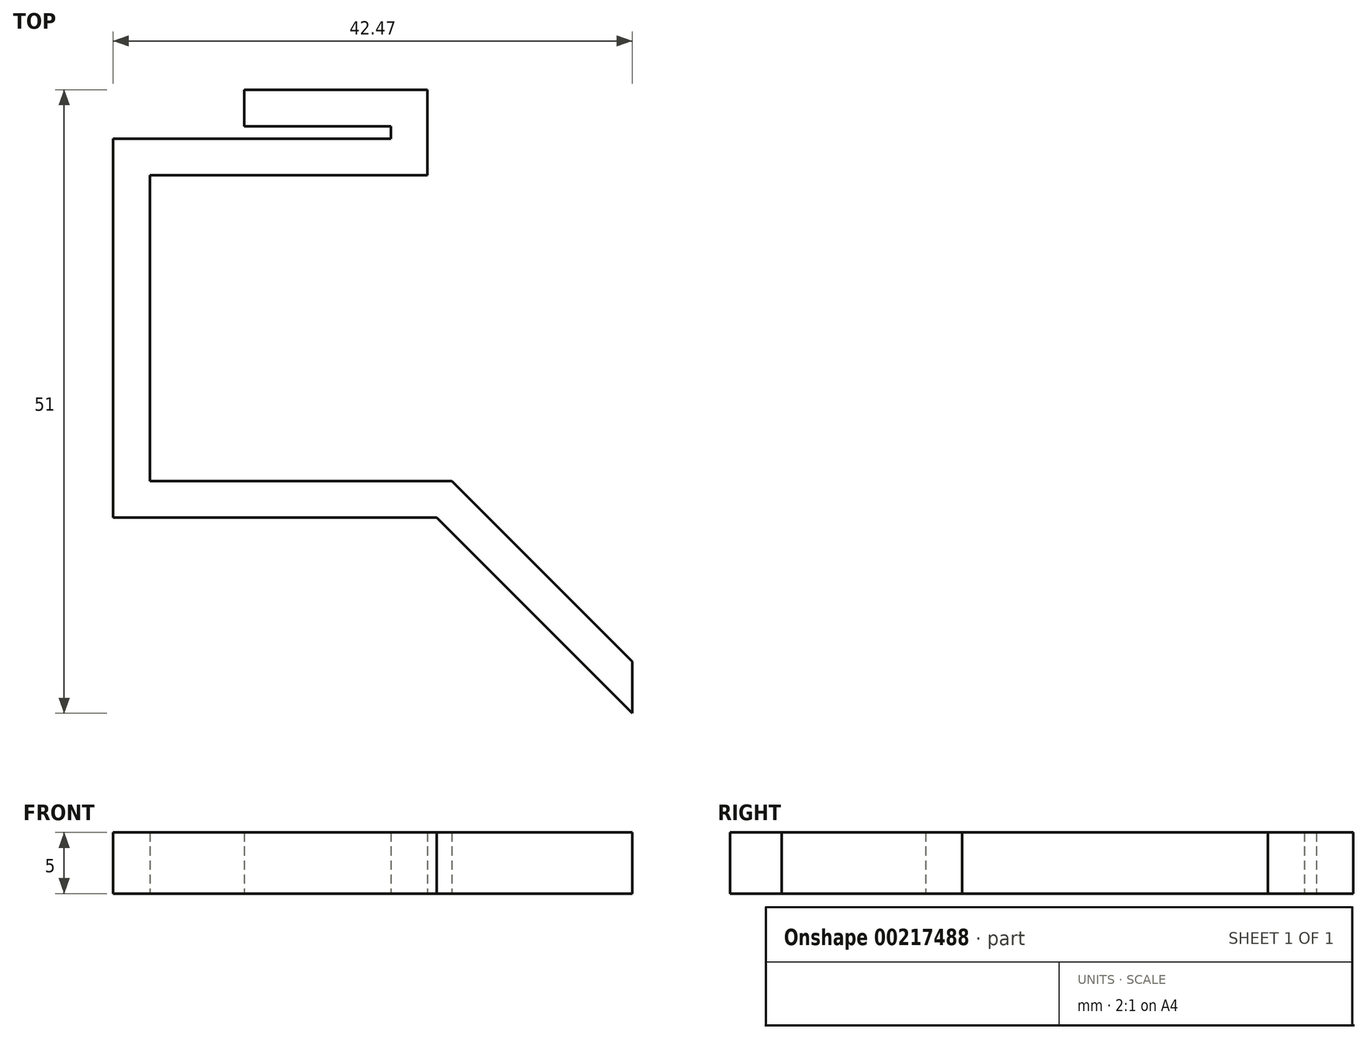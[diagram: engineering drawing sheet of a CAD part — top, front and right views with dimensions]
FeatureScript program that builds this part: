
annotation { "Feature Type Name" : "Feature", "Feature Type Description" : "" }
export const myFeature = defineFeature(function(context is Context, id is Id, definition is map)
    precondition{}
    {
        {
            var Q0;
            Q0=qCreatedBy(makeId("Top.planeOp"),FACE);
            var sketch = newSketch(context, id + "F0", { "sketchPlane" : qUnion([Q0])});
            skLineSegment(sketch, "E0", {"start": v(-24.07, 13.26) * mm, "end": v(-24.07, 6.26) * mm});
            skLineSegment(sketch, "E1", {"start": v(-24.07, 6.26) * mm, "end": v(-36.07, 6.26) * mm});
            skLineSegment(sketch, "E2", {"start": v(-36.07, -18.74) * mm, "end": v(-22.07, -18.74) * mm});
            skLineSegment(sketch, "E3", {"start": v(-22.07, -18.74) * mm, "end": v(-7.32, -33.5) * mm});
            skLineSegment(sketch, "E4", {"start": v(-7.32, -33.5) * mm, "end": v(-7.32, -37.74) * mm});
            skLineSegment(sketch, "E5", {"start": v(-7.32, -37.74) * mm, "end": v(-23.32, -21.74) * mm});
            skLineSegment(sketch, "E6", {"start": v(-23.32, -21.74) * mm, "end": v(-39.07, -21.74) * mm});
            skLineSegment(sketch, "E7", {"start": v(-24.07, 13.26) * mm, "end": v(-39.07, 13.26) * mm});
            skLineSegment(sketch, "E8", {"start": v(-39.07, 13.26) * mm, "end": v(-39.07, 10.26) * mm});
            skLineSegment(sketch, "E9", {"start": v(-39.07, 10.26) * mm, "end": v(-27.07, 10.26) * mm});
            skLineSegment(sketch, "E10", {"start": v(-27.07, 10.26) * mm, "end": v(-27.07, 9.26) * mm});
            skLineSegment(sketch, "E11", {"start": v(-27.07, 9.26) * mm, "end": v(-39.07, 9.26) * mm});
            skLineSegment(sketch, "E12", {"start": v(-36.07, 6.26) * mm, "end": v(-46.79, 6.26) * mm});
            skLineSegment(sketch, "E13", {"start": v(-46.79, 6.26) * mm, "end": v(-46.79, -18.74) * mm});
            skLineSegment(sketch, "E14", {"start": v(-46.79, -18.74) * mm, "end": v(-36.07, -18.74) * mm});
            skLineSegment(sketch, "E15", {"start": v(-39.07, 9.26) * mm, "end": v(-49.79, 9.26) * mm});
            skLineSegment(sketch, "E16", {"start": v(-49.79, 9.26) * mm, "end": v(-49.79, -21.74) * mm});
            skLineSegment(sketch, "E17", {"start": v(-49.79, -21.74) * mm, "end": v(-39.07, -21.74) * mm});
            skSolve(sketch);
        }
        {
            var Q0;
            Q0=makeQuery(id+"F0.imprint","IMPRINT",FACE,{"disambiguationData":[TD([[makeQuery(id+"F0.imprint","IMPRINT",EDGE,{"derivedFrom":sQuery(id+"F0.wireOp",EDGE,"E0")}),-1.0]])]});
            extrude(context, id + "F1", {"entities" : qUnion([Q0]), "depth" : 5 * mm});
        }
    });
